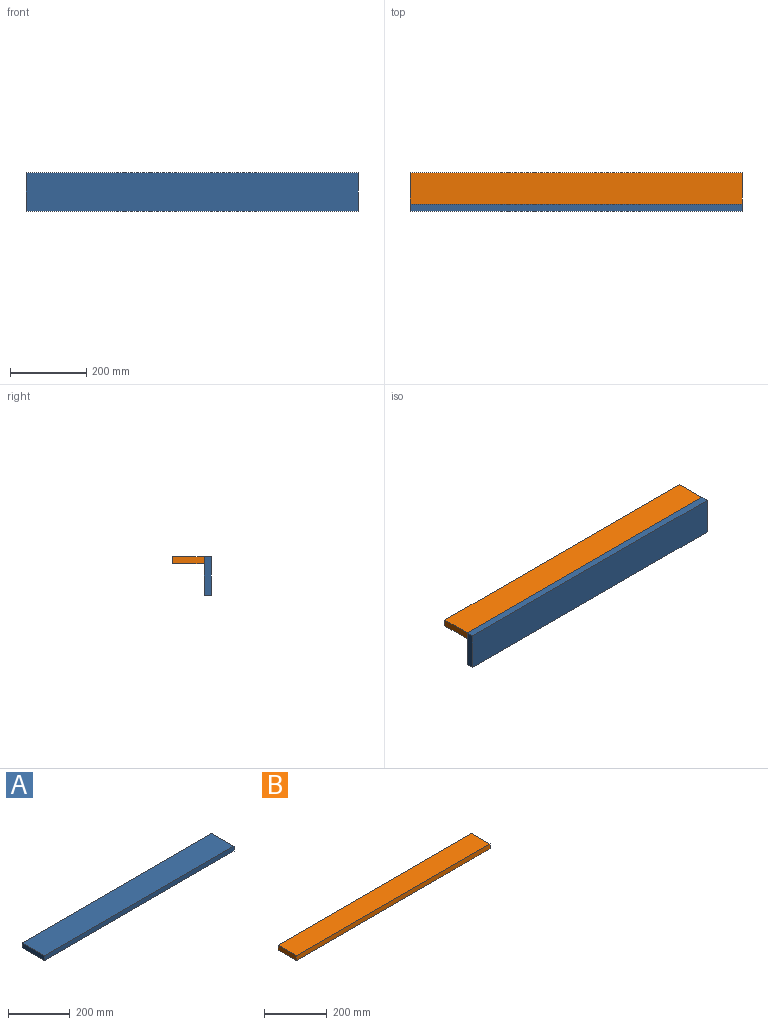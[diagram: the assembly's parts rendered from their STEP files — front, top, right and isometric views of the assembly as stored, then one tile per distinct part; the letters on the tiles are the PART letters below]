
ASSEMBLY  parts=2 mates=1
PART A: 6 faces, bbox 870x101.6x19.1 mm
  f0: plane 869.95x19.05mm, normal (0,1,0), area 16572.5mm2, adj f1,f3,f4,f5
  f1: plane 101.6x19.05mm, normal (-1,0,0), area 1935.5mm2, adj f0,f2,f4,f5
  f2: plane 869.95x19.05mm, normal (0,-1,0), area 16572.5mm2, adj f1,f3,f4,f5
  f3: plane 101.6x19.05mm, normal (1,0,0), area 1935.5mm2, adj f0,f2,f4,f5
  f4: plane 869.95x101.6mm, normal (0,0,1), area 88386.9mm2, adj f0,f1,f2,f3
  f5: plane 869.95x101.6mm, normal (0,0,-1), area 88386.9mm2, adj f0,f1,f2,f3
PART B: 6 faces, bbox 870x82.6x19.1 mm
  f0: plane 869.95x82.55mm, normal (0,0,1), area 71814.4mm2, adj f1,f2,f3,f4
  f1: plane 869.95x19.05mm, normal (0,-1,0), area 16572.5mm2, adj f0,f2,f4,f5
  f2: plane 82.55x19.05mm, normal (1,0,0), area 1572.6mm2, adj f0,f1,f3,f5
  f3: plane 869.95x19.05mm, normal (0,1,0), area 16572.5mm2, adj f0,f2,f4,f5
  f4: plane 82.55x19.05mm, normal (-1,0,0), area 1572.6mm2, adj f0,f1,f3,f5
  f5: plane 869.95x82.55mm, normal (0,0,-1), area 71814.4mm2, adj f1,f2,f3,f4
PLACE A rot(axis=(1,0,0),90deg) t=(-50.67,-68.62,-89.22)mm
PLACE B t=(-50.67,13.93,-6.67)mm
MATE fastened A.f0 <-> B.f0  axis (0,0,1) through (-485.64,-68.62,12.38)mm
